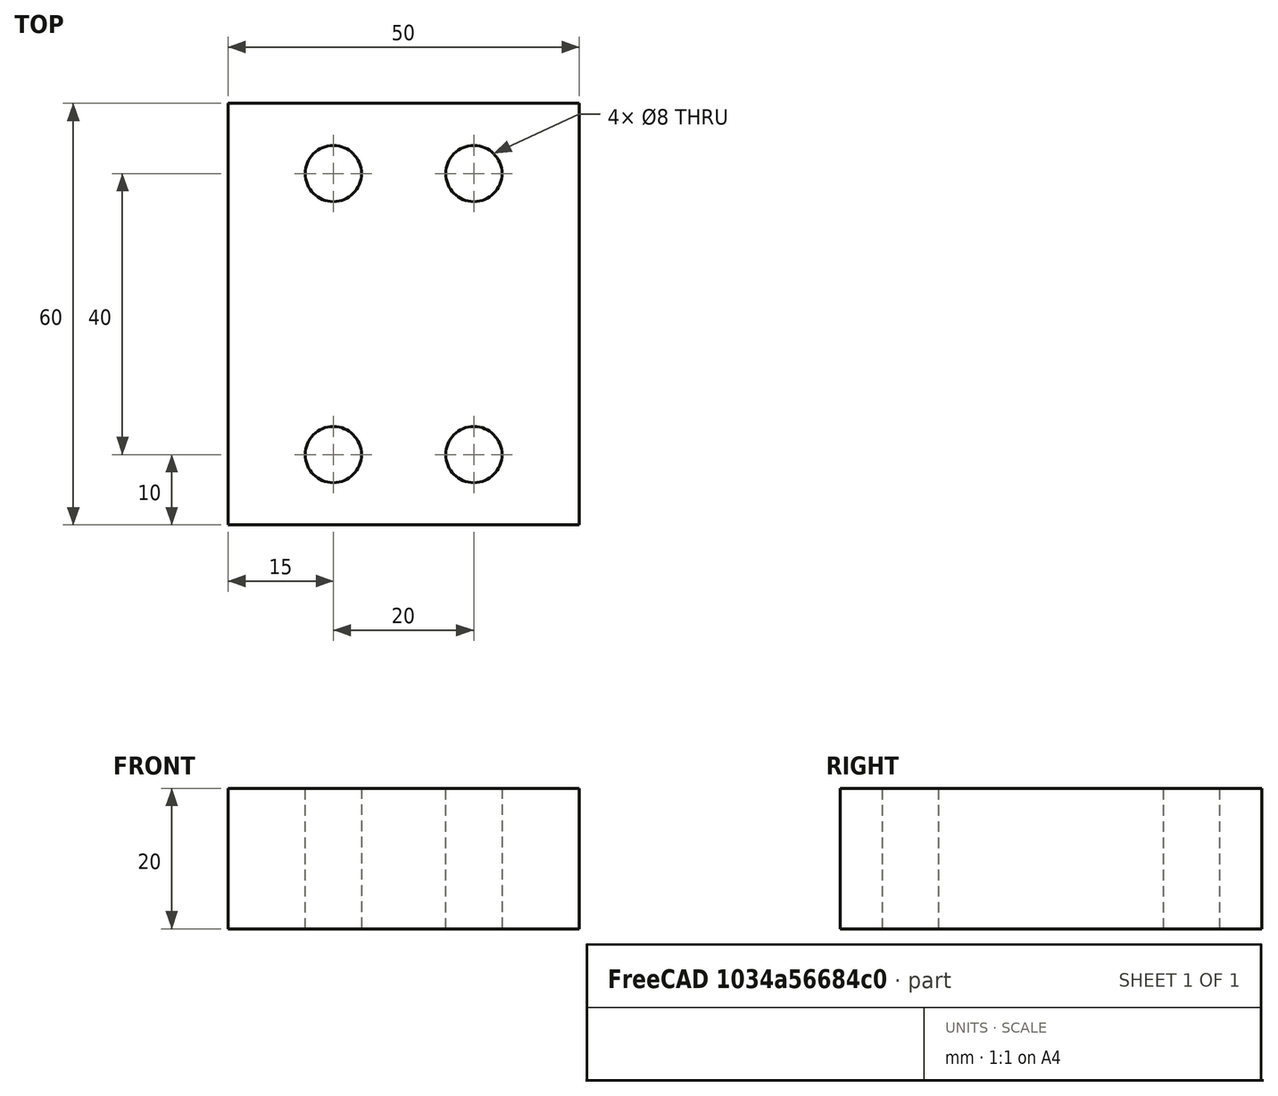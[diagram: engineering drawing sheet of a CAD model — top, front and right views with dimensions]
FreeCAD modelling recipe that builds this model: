
FCSTD DOCUMENT  (FreeCAD 0.19R17089 +1543 (Git))
Label: import-link
License: All rights reserved
LicenseURL: http://en.wikipedia.org/wiki/All_rights_reserved
objects: App::FeaturePython×40, Part::FeaturePython×40, App::Link×10, App::LinkElement×8, Sketcher::SketchObject×1, PartDesign::Pad×1, PartDesign::Body×1, App::DocumentObjectGroup×1
note: 40 computed .brp shape members not serialized (recipe doc carries the construction recipe); baked Part::Feature solids carry a one-line shape summary decoded from their .brp
EXTERNAL_REF file=xrepo-lib-003.FCStd obj=Assembly
EXTERNAL_REF file=xrepo-lib-003.FCStd obj=Assembly001
EXTERNAL_REF file=xrepo-lib-003.FCStd obj=Assembly002

FEATURE [Sketcher::SketchObject] Sketch006
  MapMode = 5
  Support = -> [XY_Plane003]
  sketch-geometry (8):
    g0: Circle CenterX=-10 CenterY=20 CenterZ=0 NormalX=0 NormalY=0 NormalZ=1 AngleXU=0 Radius=4
    g1: Circle CenterX=10 CenterY=20 CenterZ=0 NormalX=0 NormalY=0 NormalZ=1 AngleXU=0 Radius=4
    g2: Circle CenterX=10 CenterY=-20 CenterZ=0 NormalX=0 NormalY=0 NormalZ=1 AngleXU=0 Radius=4
    g3: Circle CenterX=-10 CenterY=-20 CenterZ=0 NormalX=0 NormalY=0 NormalZ=1 AngleXU=0 Radius=4
    g4: LineSegment StartX=-25 StartY=30 StartZ=0 EndX=25 EndY=30 EndZ=0
    g5: LineSegment StartX=25 StartY=30 StartZ=0 EndX=25 EndY=-30 EndZ=0
    g6: LineSegment StartX=25 StartY=-30 StartZ=0 EndX=-25 EndY=-30 EndZ=0
    g7: LineSegment StartX=-25 StartY=-30 StartZ=0 EndX=-25 EndY=30 EndZ=0
  constraints (19):
    c: Equal(g0,g1)
    c: Equal(g1,g2)
    c: Equal(g2,g3)
    c: Diameter(g0) = 8  'BHD'
    c: Symmetric(g0,g1,g-2)
    c: Symmetric(g1,g2,g-1)
    c: Symmetric(g0,g3,g-1)
    c: Coincident(g4,g5)
    c: Coincident(g5,g6)
    c: Coincident(g6,g7)
    c: Coincident(g7,g4)
    c: Horizontal(g6)
    c: Vertical(g7)
    c: Symmetric(g4,g4,g-2)
    c: Symmetric(g4,g5,g-1)
    c: Distance(g3,g2) = 20  'L1'
    c: Distance(g4) = 50  'L2'
    c: Distance(g1,g2) = 40  'W1'
    c: Distance(g7) = 60  'W2'
FEATURE [PartDesign::Pad] Pad005
  ClaimChildren = false
  Length = 20
  Length2 = 100
  Profile = -> Sketch006
  Reversed = true
  Type = 0
FEATURE [PartDesign::Body] Body003
  Group = -> [Sketch006,Pad005]
  Origin = -> Origin003
  Tip = -> Pad005
FEATURE [App::FeaturePython] Constraints003  # WARN: FeaturePython — macro-defined, semantics opaque (R4)
  GroupMode = 1
  _Version = 1
FEATURE [Part::FeaturePython] Parts003  # WARN: FeaturePython — macro-defined, semantics opaque (R4)
  Group = -> [Body003]
  GroupMode = 0
FEATURE [App::Link] Link  label="Assembly000 001"
  LinkPlacement = pos=(0,0,-2) rot=(0,0,1;0rad)
  LinkedObject = -> Link007
  Placement = pos=(0,0,-2) rot=(0,0,1;0rad)
FEATURE [App::Link] Link001  label="Assembly001 001"
  LinkedObject = -> Link008
FEATURE [Part::FeaturePython] Parts004  # WARN: FeaturePython — macro-defined, semantics opaque (R4)
  Group = -> [Link,Link001]
  GroupMode = 0
FEATURE [App::Link] Link002  label="Assembly000 002"
  LinkedObject = -> Link007
FEATURE [App::Link] Link003  label="Assembly002 001"
  LinkPlacement = pos=(0,0,2) rot=(0,0,1;0rad)
  LinkedObject = -> Link009
  Placement = pos=(0,0,2) rot=(0,0,1;0rad)
FEATURE [Part::FeaturePython] Parts005  # WARN: FeaturePython — macro-defined, semantics opaque (R4)
  Group = -> [Link002,Link003]
  GroupMode = 0
FEATURE [App::Link] Link004  label="Assembly003 001"
  LinkedObject = -> Assembly003
FEATURE [App::LinkElement] Link005_i0
  LinkPlacement = pos=(-10,20,0) rot=(0,0,1;0rad)
  LinkedObject = -> Assembly005
  Placement = pos=(-10,20,0) rot=(0,0,1;0rad)
FEATURE [App::LinkElement] Link005_i1
  LinkPlacement = pos=(10,20,0) rot=(0,0,1;0rad)
  LinkedObject = -> Assembly005
  Placement = pos=(10,20,0) rot=(0,0,1;0rad)
FEATURE [App::LinkElement] Link005_i2
  LinkPlacement = pos=(10,-20,0) rot=(0,0,1;0rad)
  LinkedObject = -> Assembly005
  Placement = pos=(10,-20,0) rot=(0,0,1;0rad)
FEATURE [App::LinkElement] Link005_i3
  LinkPlacement = pos=(-10,-20,0) rot=(0,0,1;0rad)
  LinkedObject = -> Assembly005
  Placement = pos=(-10,-20,0) rot=(0,0,1;0rad)
FEATURE [App::Link] Link005  label="Assembly005 001"
  ElementCount = 4
  ElementList = -> [Link005_i0,Link005_i1,Link005_i2,Link005_i3]
  LinkedObject = -> Assembly005
FEATURE [App::LinkElement] Link006_i0
  LinkPlacement = pos=(10,20,-33) rot=(0,-1,0;0rad)
  LinkedObject = -> Assembly004
  Placement = pos=(10,20,-33) rot=(0,-1,0;0rad)
FEATURE [App::LinkElement] Link006_i1
  LinkPlacement = pos=(-10,20,-33) rot=(0,-1,0;0rad)
  LinkedObject = -> Assembly004
  Placement = pos=(-10,20,-33) rot=(0,-1,0;0rad)
FEATURE [App::LinkElement] Link006_i2
  LinkPlacement = pos=(-10,-20,-33) rot=(0,-1,0;0rad)
  LinkedObject = -> Assembly004
  Placement = pos=(-10,-20,-33) rot=(0,-1,0;0rad)
FEATURE [App::LinkElement] Link006_i3
  LinkPlacement = pos=(10,-20,-33) rot=(0,-1,0;0rad)
  LinkedObject = -> Assembly004
  Placement = pos=(10,-20,-33) rot=(0,-1,0;0rad)
FEATURE [App::Link] Link006  label="Assembly004 001"
  ElementCount = 4
  ElementList = -> [Link006_i0,Link006_i1,Link006_i2,Link006_i3]
  LinkPlacement = pos=(8.1e-13,6.55651e-06,-55) rot=(0,1,0;3.14159rad)
  LinkedObject = -> Assembly004
  Placement = pos=(8.1e-13,6.55651e-06,-55) rot=(0,1,0;3.14159rad)
FEATURE [Part::FeaturePython] Parts006  # WARN: FeaturePython — macro-defined, semantics opaque (R4)
  Group = -> [Link004,Link005,Link006]
  GroupMode = 0
FEATURE [App::Link] Link007  label="Assembly000 003"
  LinkedObject = -> <external xrepo-lib-003.FCStd>#Assembly
FEATURE [App::Link] Link008  label="Assembly001 002"
  LinkedObject = -> <external xrepo-lib-003.FCStd>#Assembly001
FEATURE [App::Link] Link009  label="Assembly002 002"
  LinkedObject = -> <external xrepo-lib-003.FCStd>#Assembly002
FEATURE [App::DocumentObjectGroup] Group  label="Repository"
  Group = -> [Link007,Link008,Link009,Assembly003,Assembly004,Assembly005]
FEATURE [Part::FeaturePython] Assembly003  label="Assembly003 000"  # WARN: FeaturePython — macro-defined, semantics opaque (R4)
  AutoRelax = true
  BuildShape = 0
  Freeze = false
  Group = -> [Constraints003,Elements003,Parts003]
  GroupMode = 1
  SolverType = 1
  Verbose = false
  _SolverType = 1
  _Version = 1
FEATURE [App::FeaturePython] Elements003  # WARN: FeaturePython — macro-defined, semantics opaque (R4)
  Group = -> [Element005,Element006,Element007,Element008,Element009,Element010,Element011,Element012,Element015]
  GroupMode = 1
FEATURE [Part::FeaturePython] Element005  # link proxy (typed FeaturePython)
  Detach = false
  LinkTransform = true
  LinkedObject = -> Body003 [Pad005.Edge23]
  _Parent = -> Elements003
FEATURE [Part::FeaturePython] Element006  # link proxy (typed FeaturePython)
  Detach = false
  LinkTransform = true
  LinkedObject = -> Body003 [Pad005.Edge20]
  _Parent = -> Elements003
FEATURE [Part::FeaturePython] Element007  # link proxy (typed FeaturePython)
  Detach = false
  LinkTransform = true
  LinkedObject = -> Body003 [Pad005.Edge17]
  _Parent = -> Elements003
FEATURE [Part::FeaturePython] Element008  # link proxy (typed FeaturePython)
  Detach = false
  LinkTransform = true
  LinkedObject = -> Body003 [Pad005.Edge14]
  _Parent = -> Elements003
FEATURE [Part::FeaturePython] Element009  # link proxy (typed FeaturePython)
  Detach = false
  LinkTransform = true
  LinkedObject = -> Body003 [Pad005.Edge24]
  _Parent = -> Elements003
FEATURE [Part::FeaturePython] Element010  # link proxy (typed FeaturePython)
  Detach = false
  LinkTransform = true
  LinkedObject = -> Body003 [Pad005.Edge21]
  _Parent = -> Elements003
FEATURE [Part::FeaturePython] Element011  # link proxy (typed FeaturePython)
  Detach = false
  LinkTransform = true
  LinkedObject = -> Body003 [Pad005.Edge18]
  _Parent = -> Elements003
FEATURE [Part::FeaturePython] Element012  # link proxy (typed FeaturePython)
  Detach = false
  LinkTransform = true
  LinkedObject = -> Body003 [Pad005.Edge15]
  _Parent = -> Elements003
FEATURE [Part::FeaturePython] Assembly004  label="Assembly004 000"  # WARN: FeaturePython — macro-defined, semantics opaque (R4)
  AutoRelax = true
  BuildShape = 0
  Freeze = false
  Group = -> [Constraints004,Elements004,Parts004]
  GroupMode = 1
  SolverType = 1
  Verbose = false
  _SolverType = 1
  _Version = 1
FEATURE [App::FeaturePython] Constraints004  # WARN: FeaturePython — macro-defined, semantics opaque (R4)
  Group = -> [Constraint]
  GroupMode = 1
  _Version = 1
FEATURE [App::FeaturePython] Elements004  # WARN: FeaturePython — macro-defined, semantics opaque (R4)
  Group = -> [_Element,_Element001,Element013]
  GroupMode = 1
FEATURE [App::FeaturePython] Constraint  label="PlaneCoincident"  # WARN: FeaturePython — macro-defined, semantics opaque (R4)
  Angle = 0
  AnglePitch = 0
  AngleRoll = 0
  Cascade = false
  ConstraintType = 2
  Disabled = false
  Group = -> [ElementLink,ElementLink001]
  GroupMode = 1
  LockAngle = false
  Multiply = false
  OffsetX = 0
  OffsetY = 0
  _ConstraintType = 35
  _Parent = -> Constraints004
FEATURE [App::FeaturePython] ElementLink  label="_Element"  # link proxy (typed FeaturePython)
  LinkTransform = true
  LinkedObject = -> _Element
  _Parent = -> Constraint
FEATURE [Part::FeaturePython] _Element  # link proxy (typed FeaturePython)
  Detach = false
  LinkTransform = true
  LinkedObject = -> Link001 [1.$Element002.]
  _Parent = -> Elements004
FEATURE [App::FeaturePython] ElementLink001  label="_Element001"  # link proxy (typed FeaturePython)
  LinkTransform = true
  LinkedObject = -> _Element001
  _Parent = -> Constraint
FEATURE [Part::FeaturePython] _Element001  # link proxy (typed FeaturePython)
  Detach = false
  LinkTransform = true
  LinkedObject = -> Link [1.$Element001.]
  _Parent = -> Elements004
FEATURE [Part::FeaturePython] Element013  # link proxy (typed FeaturePython)
  Detach = false
  LinkTransform = true
  LinkedObject = -> Link [1.$Element.]
  _Parent = -> Elements004
FEATURE [Part::FeaturePython] Assembly005  label="Assembly005 000"  # WARN: FeaturePython — macro-defined, semantics opaque (R4)
  AutoRelax = true
  BuildShape = 0
  Freeze = false
  Group = -> [Constraints005,Elements005,Parts005]
  GroupMode = 1
  SolverType = 1
  Verbose = false
  _SolverType = 1
  _Version = 1
FEATURE [App::FeaturePython] Constraints005  # WARN: FeaturePython — macro-defined, semantics opaque (R4)
  Group = -> [Constraint001]
  GroupMode = 1
  _Version = 1
FEATURE [App::FeaturePython] Elements005  # WARN: FeaturePython — macro-defined, semantics opaque (R4)
  Group = -> [_Element002,_Element003,Element014]
  GroupMode = 1
FEATURE [App::FeaturePython] Constraint001  label="PlaneCoincident001"  # WARN: FeaturePython — macro-defined, semantics opaque (R4)
  Angle = 0
  AnglePitch = 0
  AngleRoll = 0
  Cascade = false
  ConstraintType = 2
  Disabled = false
  Group = -> [ElementLink002,ElementLink003]
  GroupMode = 1
  LockAngle = false
  Multiply = false
  OffsetX = 0
  OffsetY = 0
  _ConstraintType = 35
  _Parent = -> Constraints005
FEATURE [App::FeaturePython] ElementLink002  label="_Element002"  # link proxy (typed FeaturePython)
  LinkTransform = true
  LinkedObject = -> _Element002
  _Parent = -> Constraint001
FEATURE [Part::FeaturePython] _Element002  # link proxy (typed FeaturePython)
  Detach = false
  LinkTransform = true
  LinkedObject = -> Link002 [1.$Element001.]
  _Parent = -> Elements005
FEATURE [App::FeaturePython] ElementLink003  label="_Element003"  # link proxy (typed FeaturePython)
  LinkTransform = true
  LinkedObject = -> _Element003
  _Parent = -> Constraint001
FEATURE [Part::FeaturePython] _Element003  # link proxy (typed FeaturePython)
  Detach = false
  LinkTransform = true
  LinkedObject = -> Link003 [1.$Element004.]
  _Parent = -> Elements005
FEATURE [Part::FeaturePython] Element014  # link proxy (typed FeaturePython)
  Detach = false
  LinkTransform = true
  LinkedObject = -> Link002 [1.$Element.]
  _Parent = -> Elements005
FEATURE [Part::FeaturePython] Assembly006  label="Assembly006 000"  # WARN: FeaturePython — macro-defined, semantics opaque (R4)
  AutoRelax = true
  BuildShape = 0
  Freeze = false
  Group = -> [Constraints006,Elements006,Parts006]
  GroupMode = 1
  SolverType = 1
  Verbose = false
  _SolverType = 1
  _Version = 1
FEATURE [App::FeaturePython] Constraints006  # WARN: FeaturePython — macro-defined, semantics opaque (R4)
  Group = -> [Constraint002,Constraint003,Constraint004,Constraint005,Constraint006,Constraint007,Constraint008,Constraint009,Constraint010]
  GroupMode = 1
  _Version = 1
FEATURE [App::FeaturePython] Elements006  # WARN: FeaturePython — macro-defined, semantics opaque (R4)
  Group = -> [_Element004,_Element005,_Element006,_Element007,_Element008,_Element009,_Element010,_Element011,_Element012,_Element013,_Element014,_Element015,_Element016,_Element017,_Element018,_Element019,_Element020]
  GroupMode = 1
FEATURE [App::FeaturePython] Constraint002  label="Locked"  # WARN: FeaturePython — macro-defined, semantics opaque (R4)
  ConstraintType = 0
  Disabled = false
  Group = -> [ElementLink004]
  GroupMode = 1
  _ConstraintType = 0
  _Parent = -> Constraints006
FEATURE [App::FeaturePython] ElementLink004  label="_Element004"  # link proxy (typed FeaturePython)
  LinkTransform = true
  LinkedObject = -> _Element004
  _Parent = -> Constraint002
FEATURE [Part::FeaturePython] Element015  # link proxy (typed FeaturePython)
  Detach = false
  LinkTransform = true
  LinkedObject = -> Body003 [Pad005.Face9]
  _Parent = -> Elements003
FEATURE [Part::FeaturePython] _Element004  # link proxy (typed FeaturePython)
  Detach = false
  LinkTransform = true
  LinkedObject = -> Link004 [1.$Element015.]
  _Parent = -> Elements006
FEATURE [App::FeaturePython] Constraint003  label="PlaneCoincident002"  # WARN: FeaturePython — macro-defined, semantics opaque (R4)
  Angle = 0
  AnglePitch = 0
  AngleRoll = 0
  Cascade = false
  ConstraintType = 2
  Disabled = false
  Group = -> [ElementLink005,ElementLink006]
  GroupMode = 1
  LockAngle = false
  Multiply = false
  OffsetX = 0
  OffsetY = 0
  _ConstraintType = 35
  _Parent = -> Constraints006
FEATURE [App::FeaturePython] ElementLink005  label="_Element005"  # link proxy (typed FeaturePython)
  LinkTransform = true
  LinkedObject = -> _Element005
  _Parent = -> Constraint003
FEATURE [Part::FeaturePython] _Element005  # link proxy (typed FeaturePython)
  Detach = false
  LinkTransform = true
  LinkedObject = -> Link005 [Link005_i0.1.$Element014.]
  _Parent = -> Elements006
FEATURE [App::FeaturePython] ElementLink006  label="_Element006"  # link proxy (typed FeaturePython)
  LinkTransform = true
  LinkedObject = -> _Element006
  _Parent = -> Constraint003
FEATURE [Part::FeaturePython] _Element006  # link proxy (typed FeaturePython)
  Detach = false
  LinkTransform = true
  LinkedObject = -> Link004 [1.$Element005.]
  _Parent = -> Elements006
FEATURE [App::FeaturePython] Constraint004  label="PlaneCoincident003"  # WARN: FeaturePython — macro-defined, semantics opaque (R4)
  Angle = 0
  AnglePitch = 0
  AngleRoll = 0
  Cascade = false
  ConstraintType = 2
  Disabled = false
  Group = -> [ElementLink007,ElementLink008]
  GroupMode = 1
  LockAngle = false
  Multiply = false
  OffsetX = 0
  OffsetY = 0
  _ConstraintType = 35
  _Parent = -> Constraints006
FEATURE [App::FeaturePython] ElementLink007  label="_Element007"  # link proxy (typed FeaturePython)
  LinkTransform = true
  LinkedObject = -> _Element007
  _Parent = -> Constraint004
FEATURE [Part::FeaturePython] _Element007  # link proxy (typed FeaturePython)
  Detach = false
  LinkTransform = true
  LinkedObject = -> Link004 [1.$Element006.]
  _Parent = -> Elements006
FEATURE [App::FeaturePython] ElementLink008  label="_Element008"  # link proxy (typed FeaturePython)
  LinkTransform = true
  LinkedObject = -> _Element008
  _Parent = -> Constraint004
FEATURE [Part::FeaturePython] _Element008  # link proxy (typed FeaturePython)
  Detach = false
  LinkTransform = true
  LinkedObject = -> Link005 [Link005_i1.1.$Element014.]
  _Parent = -> Elements006
FEATURE [App::FeaturePython] Constraint005  label="PlaneCoincident004"  # WARN: FeaturePython — macro-defined, semantics opaque (R4)
  Angle = 0
  AnglePitch = 0
  AngleRoll = 0
  Cascade = false
  ConstraintType = 2
  Disabled = false
  Group = -> [ElementLink009,ElementLink010]
  GroupMode = 1
  LockAngle = false
  Multiply = false
  OffsetX = 0
  OffsetY = 0
  _ConstraintType = 35
  _Parent = -> Constraints006
FEATURE [App::FeaturePython] ElementLink009  label="_Element009"  # link proxy (typed FeaturePython)
  LinkTransform = true
  LinkedObject = -> _Element009
  _Parent = -> Constraint005
FEATURE [Part::FeaturePython] _Element009  # link proxy (typed FeaturePython)
  Detach = false
  LinkTransform = true
  LinkedObject = -> Link004 [1.$Element007.]
  _Parent = -> Elements006
FEATURE [App::FeaturePython] ElementLink010  label="_Element010"  # link proxy (typed FeaturePython)
  LinkTransform = true
  LinkedObject = -> _Element010
  _Parent = -> Constraint005
FEATURE [Part::FeaturePython] _Element010  # link proxy (typed FeaturePython)
  Detach = false
  LinkTransform = true
  LinkedObject = -> Link005 [Link005_i2.1.$Element014.]
  _Parent = -> Elements006
FEATURE [App::FeaturePython] Constraint006  label="PlaneCoincident005"  # WARN: FeaturePython — macro-defined, semantics opaque (R4)
  Angle = 0
  AnglePitch = 0
  AngleRoll = 0
  Cascade = false
  ConstraintType = 2
  Disabled = false
  Group = -> [ElementLink011,ElementLink012]
  GroupMode = 1
  LockAngle = false
  Multiply = false
  OffsetX = 0
  OffsetY = 0
  _ConstraintType = 35
  _Parent = -> Constraints006
FEATURE [App::FeaturePython] ElementLink011  label="_Element011"  # link proxy (typed FeaturePython)
  LinkTransform = true
  LinkedObject = -> _Element011
  _Parent = -> Constraint006
FEATURE [Part::FeaturePython] _Element011  # link proxy (typed FeaturePython)
  Detach = false
  LinkTransform = true
  LinkedObject = -> Link004 [1.$Element008.]
  _Parent = -> Elements006
FEATURE [App::FeaturePython] ElementLink012  label="_Element012"  # link proxy (typed FeaturePython)
  LinkTransform = true
  LinkedObject = -> _Element012
  _Parent = -> Constraint006
FEATURE [Part::FeaturePython] _Element012  # link proxy (typed FeaturePython)
  Detach = false
  LinkTransform = true
  LinkedObject = -> Link005 [Link005_i3.1.$Element014.]
  _Parent = -> Elements006
FEATURE [App::FeaturePython] Constraint007  label="PlaneCoincident006"  # WARN: FeaturePython — macro-defined, semantics opaque (R4)
  Angle = 0
  AnglePitch = 0
  AngleRoll = 0
  Cascade = false
  ConstraintType = 2
  Disabled = false
  Group = -> [ElementLink013,ElementLink014]
  GroupMode = 1
  LockAngle = false
  Multiply = false
  OffsetX = 0
  OffsetY = 0
  _ConstraintType = 35
  _Parent = -> Constraints006
FEATURE [App::FeaturePython] ElementLink013  label="_Element013"  # link proxy (typed FeaturePython)
  LinkTransform = true
  LinkedObject = -> _Element013
  _Parent = -> Constraint007
FEATURE [Part::FeaturePython] _Element013  # link proxy (typed FeaturePython)
  Detach = false
  LinkTransform = true
  LinkedObject = -> Link004 [1.$Element009.]
  _Parent = -> Elements006
FEATURE [App::FeaturePython] ElementLink014  label="_Element014"  # link proxy (typed FeaturePython)
  LinkTransform = true
  LinkedObject = -> _Element014
  _Parent = -> Constraint007
FEATURE [Part::FeaturePython] _Element014  # link proxy (typed FeaturePython)
  Detach = false
  LinkTransform = true
  LinkedObject = -> Link006 [Link006_i0.1.$Element013.]
  _Parent = -> Elements006
FEATURE [App::FeaturePython] Constraint008  label="PlaneCoincident007"  # WARN: FeaturePython — macro-defined, semantics opaque (R4)
  Angle = 0
  AnglePitch = 0
  AngleRoll = 0
  Cascade = false
  ConstraintType = 2
  Disabled = false
  Group = -> [ElementLink015,ElementLink016]
  GroupMode = 1
  LockAngle = false
  Multiply = false
  OffsetX = 0
  OffsetY = 0
  _ConstraintType = 35
  _Parent = -> Constraints006
FEATURE [App::FeaturePython] ElementLink015  label="_Element015"  # link proxy (typed FeaturePython)
  LinkTransform = true
  LinkedObject = -> _Element015
  _Parent = -> Constraint008
FEATURE [Part::FeaturePython] _Element015  # link proxy (typed FeaturePython)
  Detach = false
  LinkTransform = true
  LinkedObject = -> Link004 [1.$Element010.]
  _Parent = -> Elements006
FEATURE [App::FeaturePython] ElementLink016  label="_Element016"  # link proxy (typed FeaturePython)
  LinkTransform = true
  LinkedObject = -> _Element016
  _Parent = -> Constraint008
FEATURE [Part::FeaturePython] _Element016  # link proxy (typed FeaturePython)
  Detach = false
  LinkTransform = true
  LinkedObject = -> Link006 [Link006_i1.1.$Element013.]
  _Parent = -> Elements006
FEATURE [App::FeaturePython] Constraint009  label="PlaneCoincident008"  # WARN: FeaturePython — macro-defined, semantics opaque (R4)
  Angle = 0
  AnglePitch = 0
  AngleRoll = 0
  Cascade = false
  ConstraintType = 2
  Disabled = false
  Group = -> [ElementLink017,ElementLink018]
  GroupMode = 1
  LockAngle = false
  Multiply = false
  OffsetX = 0
  OffsetY = 0
  _ConstraintType = 35
  _Parent = -> Constraints006
FEATURE [App::FeaturePython] ElementLink017  label="_Element017"  # link proxy (typed FeaturePython)
  LinkTransform = true
  LinkedObject = -> _Element017
  _Parent = -> Constraint009
FEATURE [Part::FeaturePython] _Element017  # link proxy (typed FeaturePython)
  Detach = false
  LinkTransform = true
  LinkedObject = -> Link004 [1.$Element011.]
  _Parent = -> Elements006
FEATURE [App::FeaturePython] ElementLink018  label="_Element018"  # link proxy (typed FeaturePython)
  LinkTransform = true
  LinkedObject = -> _Element018
  _Parent = -> Constraint009
FEATURE [Part::FeaturePython] _Element018  # link proxy (typed FeaturePython)
  Detach = false
  LinkTransform = true
  LinkedObject = -> Link006 [Link006_i2.1.$Element013.]
  _Parent = -> Elements006
FEATURE [App::FeaturePython] Constraint010  label="PlaneCoincident009"  # WARN: FeaturePython — macro-defined, semantics opaque (R4)
  Angle = 0
  AnglePitch = 0
  AngleRoll = 0
  Cascade = false
  ConstraintType = 2
  Disabled = false
  Group = -> [ElementLink019,ElementLink020]
  GroupMode = 1
  LockAngle = false
  Multiply = false
  OffsetX = 0
  OffsetY = 0
  _ConstraintType = 35
  _Parent = -> Constraints006
FEATURE [App::FeaturePython] ElementLink019  label="_Element019"  # link proxy (typed FeaturePython)
  LinkTransform = true
  LinkedObject = -> _Element019
  _Parent = -> Constraint010
FEATURE [Part::FeaturePython] _Element019  # link proxy (typed FeaturePython)
  Detach = false
  LinkTransform = true
  LinkedObject = -> Link004 [1.$Element012.]
  _Parent = -> Elements006
FEATURE [App::FeaturePython] ElementLink020  label="_Element020"  # link proxy (typed FeaturePython)
  LinkTransform = true
  LinkedObject = -> _Element020
  _Parent = -> Constraint010
FEATURE [Part::FeaturePython] _Element020  # link proxy (typed FeaturePython)
  Detach = false
  LinkTransform = true
  LinkedObject = -> Link006 [Link006_i3.1.$Element013.]
  _Parent = -> Elements006

RESOLVED EXTERNAL PARTS (link-assembly join: the EXTERNAL_REF files above that resolve inside this repo's crawl, each included once):
---- part xrepo-lib-003.FCStd = doc fcstd_cd6cd5374638 ----
FCSTD DOCUMENT  (FreeCAD 0.19R17089 +1543 (Git))
Label: xrepo-lib-003
License: All rights reserved
LicenseURL: http://en.wikipedia.org/wiki/All_rights_reserved
objects: Part::FeaturePython×14, Sketcher::SketchObject×9, App::FeaturePython×8, PartDesign::Pad×8, PartDesign::Body×4, PartDesign::Chamfer×2, PartDesign::Pocket×1
note: 43 computed .brp shape members not serialized (recipe doc carries the construction recipe); baked Part::Feature solids carry a one-line shape summary decoded from their .brp

FEATURE [App::FeaturePython] Constraints  # WARN: FeaturePython — macro-defined, semantics opaque (R4)
  GroupMode = 1
  _Version = 1
FEATURE [Sketcher::SketchObject] Sketch
  MapMode = 5
  Support = -> [XY_Plane]
  sketch-geometry (2):
    g0: Circle CenterX=0 CenterY=0 CenterZ=0 NormalX=0 NormalY=0 NormalZ=1 AngleXU=0 Radius=4.15
    g1: Circle CenterX=0 CenterY=0 CenterZ=0 NormalX=0 NormalY=0 NormalZ=1 AngleXU=0 Radius=8
  constraints (4):
    c: Coincident(g0,g-1)
    c: Coincident(g1,g0)
    c: Diameter(g0) = 8.3  'D1'
    c: Diameter(g1) = 16  'D2'
FEATURE [PartDesign::Pad] Pad
  ClaimChildren = false
  Length = 2
  Length2 = 100
  Profile = -> Sketch
  Type = 0
FEATURE [PartDesign::Body] Body
  Group = -> [Sketch,Pad]
  Origin = -> Origin
  Tip = -> Pad
FEATURE [Part::FeaturePython] Parts  # WARN: FeaturePython — macro-defined, semantics opaque (R4)
  Group = -> [Body]
  GroupMode = 0
FEATURE [App::FeaturePython] Constraints001  # WARN: FeaturePython — macro-defined, semantics opaque (R4)
  GroupMode = 1
  _Version = 1
FEATURE [Sketcher::SketchObject] Sketch001
  MapMode = 5
  Support = -> [XY_Plane001]
  sketch-geometry (8):
    g0: Circle CenterX=0 CenterY=0 CenterZ=0 NormalX=0 NormalY=0 NormalZ=1 AngleXU=0 Radius=4
    g1: LineSegment StartX=7.50496 StartY=0.0945881 StartZ=0 EndX=3.67056 EndY=6.54678 EndZ=0
    g2: LineSegment StartX=3.67056 StartY=6.54678 StartZ=0 EndX=-3.83439 EndY=6.45219 EndZ=0
    g3: LineSegment StartX=-3.83439 StartY=6.45219 StartZ=0 EndX=-7.50496 EndY=-0.0945881 EndZ=0
    g4: LineSegment StartX=-7.50496 StartY=-0.0945881 StartZ=0 EndX=-3.67056 EndY=-6.54678 EndZ=0
    g5: LineSegment StartX=-3.67056 StartY=-6.54678 StartZ=0 EndX=3.83439 EndY=-6.45219 EndZ=0
    g6: LineSegment StartX=3.83439 StartY=-6.45219 StartZ=0 EndX=7.50496 EndY=0.0945881 EndZ=0
    g7: Circle [constr] CenterX=0 CenterY=0 CenterZ=0 NormalX=0 NormalY=0 NormalZ=1 AngleXU=0 Radius=7.50555
  constraints (17):
    c: Coincident(g0,g-1)
    c: Diameter(g0) = 8  'D1'
    c: Coincident(g1,g2)
    c: Coincident(g2,g3)
    c: Coincident(g3,g4)
    c: Coincident(g4,g5)
    c: Coincident(g5,g6)
    c: Coincident(g6,g1)
    c: Equal(g1, g2-g6) x5
    c: PointOnObject(g1,g7)
    c: PointOnObject(g2,g7)
    c: PointOnObject(g3,g7)
    c: PointOnObject(g4,g7)
    c: PointOnObject(g5,g7)
    c: PointOnObject(g6,g7)
    c: Coincident(g7,g0)
    c: Distance(g1,g5) = 13  'WS'
FEATURE [PartDesign::Pad] Pad001
  ClaimChildren = false
  Length = 6.4
  Length2 = 100
  Profile = -> Sketch001
  Type = 0
FEATURE [PartDesign::Body] Body001
  Group = -> [Sketch001,Pad001]
  Origin = -> Origin001
  Tip = -> Pad001
FEATURE [Part::FeaturePython] Parts001  # WARN: FeaturePython — macro-defined, semantics opaque (R4)
  Group = -> [Body001]
  GroupMode = 0
FEATURE [App::FeaturePython] Constraints002  # WARN: FeaturePython — macro-defined, semantics opaque (R4)
  GroupMode = 1
  _Version = 1
FEATURE [Sketcher::SketchObject] Sketch004
  MapMode = 5
  Support = -> [XY_Plane002]
  sketch-geometry (1):
    g0: Circle CenterX=0 CenterY=0 CenterZ=0 NormalX=0 NormalY=0 NormalZ=1 AngleXU=0 Radius=6.5
  constraints (2):
    c: Coincident(g0,g-1)
    c: Diameter(g0) = 13  'DH'
FEATURE [Sketcher::SketchObject] Sketch002
  MapMode = 5
  Support = -> [XY_Plane002]
  sketch-geometry (1):
    g0: Circle CenterX=0 CenterY=0 CenterZ=0 NormalX=0 NormalY=0 NormalZ=1 AngleXU=0 Radius=4
  constraints (2):
    c: Coincident(g0,g-1)
    c: Diameter(g0) = 8  'D1'
FEATURE [PartDesign::Pad] Pad002
  ClaimChildren = false
  Length = 5
  Length2 = 100
  Profile = -> Sketch002
  Reversed = true
  Type = 0
FEATURE [Sketcher::SketchObject] Sketch003
  ExternalGeometry = -> [Pad002]
  MapMode = 5
  Placement = pos=(0,0,-5) rot=(1,0,0;3.14159rad)
  Support = -> [Pad002]
FEATURE [PartDesign::Pad] Pad003
  BaseFeature = -> Pad002
  ClaimChildren = false
  Length = 30
  Length2 = 100
  Profile = -> Sketch003
  Type = 0
FEATURE [PartDesign::Pad] Pad004
  BaseFeature = -> Pad003
  ClaimChildren = false
  Length = 6
  Length2 = 100
  Profile = -> Sketch004
  Type = 0
FEATURE [Sketcher::SketchObject] Sketch005
  MapMode = 5
  Placement = pos=(0,0,6) rot=(0,0,1;0rad)
  Support = -> [Pad004]
  sketch-geometry (7):
    g0: LineSegment StartX=3.4641 StartY=0 StartZ=0 EndX=1.73205 EndY=3 EndZ=0
    g1: LineSegment StartX=1.73205 StartY=3 StartZ=0 EndX=-1.73205 EndY=3 EndZ=0
    g2: LineSegment StartX=-1.73205 StartY=3 StartZ=0 EndX=-3.4641 EndY=0 EndZ=0
    g3: LineSegment StartX=-3.4641 StartY=0 StartZ=0 EndX=-1.73205 EndY=-3 EndZ=0
    g4: LineSegment StartX=-1.73205 StartY=-3 StartZ=0 EndX=1.73205 EndY=-3 EndZ=0
    g5: LineSegment StartX=1.73205 StartY=-3 StartZ=0 EndX=3.4641 EndY=0 EndZ=0
    g6: Circle [constr] CenterX=0 CenterY=0 CenterZ=0 NormalX=0 NormalY=0 NormalZ=1 AngleXU=0 Radius=3.4641
  constraints (16):
    c: Coincident(g0,g1)
    c: Coincident(g1,g2)
    c: Coincident(g2,g3)
    c: Coincident(g3,g4)
    c: Coincident(g4,g5)
    c: Coincident(g5,g0)
    c: Equal(g0, g1-g5) x5
    c: PointOnObject(g0,g6)
    c: PointOnObject(g1,g6)
    c: PointOnObject(g2,g6)
    c: PointOnObject(g3,g6)
    c: PointOnObject(g4,g6)
    c: PointOnObject(g5,g6)
    c: Coincident(g6,g-1)
    c: PointOnObject(g5,g-1)
    c: Distance(g0,g4) = 6  'WS'
FEATURE [PartDesign::Pocket] Pocket
  BaseFeature = -> Pad004
  ClaimChildren = false
  Length = 5
  Length2 = 100
  Profile = -> Sketch005
  Type = 0
FEATURE [PartDesign::Chamfer] Chamfer
  Base = -> Pocket [Edge6]
  BaseFeature = -> Pocket
  Size = 1.2
FEATURE [PartDesign::Body] Body002
  Group = -> [Sketch002,Pad002,Sketch003,Pad003,Sketch004,Pad004,Sketch005,Pocket,Chamfer]
  Origin = -> Origin002
  Tip = -> Chamfer
FEATURE [Part::FeaturePython] Parts002  # WARN: FeaturePython — macro-defined, semantics opaque (R4)
  Group = -> [Body002]
  GroupMode = 0
FEATURE [App::FeaturePython] Constraints003  # WARN: FeaturePython — macro-defined, semantics opaque (R4)
  GroupMode = 1
  _Version = 1
FEATURE [Sketcher::SketchObject] Sketch006
  MapMode = 5
  Support = -> [XY_Plane003]
  sketch-geometry (1):
    g0: Circle CenterX=0 CenterY=0 CenterZ=0 NormalX=0 NormalY=0 NormalZ=1 AngleXU=0 Radius=4
  constraints (2):
    c: Coincident(g0,g-1)
    c: Diameter(g0) = 8  'D1'
FEATURE [PartDesign::Pad] Pad005
  ClaimChildren = false
  Length = 5
  Length2 = 100
  Profile = -> Sketch006
  Reversed = true
  Type = 0
FEATURE [Sketcher::SketchObject] Sketch007
  ExternalGeometry = -> [Pad005]
  MapMode = 5
  Placement = pos=(0,0,-5) rot=(1,0,0;3.14159rad)
  Support = -> [Pad005]
FEATURE [PartDesign::Pad] Pad006
  BaseFeature = -> Pad005
  ClaimChildren = false
  Length = 30
  Length2 = 100
  Profile = -> Sketch007
  Type = 0
FEATURE [PartDesign::Chamfer] Chamfer001
  Base = -> Pad006 [Edge5]
  BaseFeature = -> Pad006
  Size = 1.2
FEATURE [Sketcher::SketchObject] Sketch008
  MapMode = 5
  Support = -> [XY_Plane003]
  sketch-geometry (7):
    g0: LineSegment StartX=7.50555 StartY=0 StartZ=0 EndX=3.75278 EndY=6.5 EndZ=0
    g1: LineSegment StartX=3.75278 StartY=6.5 StartZ=0 EndX=-3.75278 EndY=6.5 EndZ=0
    g2: LineSegment StartX=-3.75278 StartY=6.5 StartZ=0 EndX=-7.50555 EndY=3.3924e-11 EndZ=0
    g3: LineSegment StartX=-7.50555 StartY=3.3924e-11 StartZ=0 EndX=-3.75278 EndY=-6.5 EndZ=0
    g4: LineSegment StartX=-3.75278 StartY=-6.5 StartZ=0 EndX=3.75278 EndY=-6.5 EndZ=0
    g5: LineSegment StartX=3.75278 StartY=-6.5 StartZ=0 EndX=7.50555 EndY=0 EndZ=0
    g6: Circle [constr] CenterX=0 CenterY=0 CenterZ=0 NormalX=0 NormalY=0 NormalZ=1 AngleXU=0 Radius=7.50555
  constraints (16):
    c: Coincident(g0,g1)
    c: Coincident(g1,g2)
    c: Coincident(g2,g3)
    c: Coincident(g3,g4)
    c: Coincident(g4,g5)
    c: Coincident(g5,g0)
    c: Equal(g0, g1-g5) x5
    c: PointOnObject(g0,g6)
    c: PointOnObject(g1,g6)
    c: PointOnObject(g2,g6)
    c: PointOnObject(g3,g6)
    c: PointOnObject(g4,g6)
    c: PointOnObject(g5,g6)
    c: Coincident(g6,g-1)
    c: PointOnObject(g5,g-1)
    c: Distance(g0,g4) = 13  'WS'
FEATURE [PartDesign::Pad] Pad007
  BaseFeature = -> Chamfer001
  ClaimChildren = false
  Length = 6.4
  Length2 = 100
  Profile = -> Sketch008
  Type = 0
FEATURE [PartDesign::Body] Body003
  Group = -> [Sketch006,Pad005,Sketch007,Pad006,Chamfer001,Sketch008,Pad007]
  Origin = -> Origin003
  Tip = -> Pad007
FEATURE [Part::FeaturePython] Parts003  # WARN: FeaturePython — macro-defined, semantics opaque (R4)
  Group = -> [Body003]
  GroupMode = 0
FEATURE [Part::FeaturePython] Element  # link proxy (typed FeaturePython)
  Detach = false
  LinkTransform = true
  LinkedObject = -> Body [Pad.Edge5]
  _Parent = -> Elements
FEATURE [Part::FeaturePython] Element001  # link proxy (typed FeaturePython)
  Detach = false
  LinkTransform = true
  LinkedObject = -> Body [Pad.Edge6]
  _Parent = -> Elements
FEATURE [App::FeaturePython] Elements  # WARN: FeaturePython — macro-defined, semantics opaque (R4)
  Group = -> [Element,Element001]
  GroupMode = 1
FEATURE [Part::FeaturePython] Assembly  label="Assembly000 000"  # WARN: FeaturePython — macro-defined, semantics opaque (R4)
  AutoRelax = true
  BuildShape = 0
  Freeze = false
  Group = -> [Constraints,Elements,Parts]
  GroupMode = 1
  SolverType = 1
  Verbose = false
  _SolverType = 1
  _Version = 1
FEATURE [Part::FeaturePython] Element002  # link proxy (typed FeaturePython)
  Detach = false
  LinkTransform = true
  LinkedObject = -> Body001 [Pad001.Edge20]
  _Parent = -> Elements001
FEATURE [Part::FeaturePython] Element003  # link proxy (typed FeaturePython)
  Detach = false
  LinkTransform = true
  LinkedObject = -> Body001 [Pad001.Edge21]
  _Parent = -> Elements001
FEATURE [App::FeaturePython] Elements001  # WARN: FeaturePython — macro-defined, semantics opaque (R4)
  Group = -> [Element002,Element003]
  GroupMode = 1
FEATURE [Part::FeaturePython] Assembly001  label="Assembly001 000"  # WARN: FeaturePython — macro-defined, semantics opaque (R4)
  AutoRelax = true
  BuildShape = 0
  Freeze = false
  Group = -> [Constraints001,Elements001,Parts001]
  GroupMode = 1
  SolverType = 1
  Verbose = false
  _SolverType = 1
  _Version = 1
FEATURE [Part::FeaturePython] Element004  # link proxy (typed FeaturePython)
  Detach = false
  LinkTransform = true
  LinkedObject = -> Body002 [Pad002.Edge2]
  _Parent = -> Elements002
FEATURE [App::FeaturePython] Elements002  # WARN: FeaturePython — macro-defined, semantics opaque (R4)
  Group = -> [Element004]
  GroupMode = 1
FEATURE [Part::FeaturePython] Assembly002  label="Assembly002 000"  # WARN: FeaturePython — macro-defined, semantics opaque (R4)
  AutoRelax = true
  BuildShape = 0
  Freeze = false
  Group = -> [Constraints002,Elements002,Parts002]
  GroupMode = 1
  SolverType = 1
  Verbose = false
  _SolverType = 1
  _Version = 1
FEATURE [Part::FeaturePython] Assembly003  label="Assembly003 000"  # WARN: FeaturePython — macro-defined, semantics opaque (R4)
  AutoRelax = true
  BuildShape = 0
  Freeze = false
  Group = -> [Constraints003,Elements003,Parts003]
  GroupMode = 1
  SolverType = 1
  Verbose = false
  _SolverType = 1
  _Version = 1
FEATURE [App::FeaturePython] Elements003  # WARN: FeaturePython — macro-defined, semantics opaque (R4)
  Group = -> [Element005]
  GroupMode = 1
FEATURE [Part::FeaturePython] Element005  label="Element004"  # link proxy (typed FeaturePython)
  Detach = false
  LinkTransform = true
  LinkedObject = -> Body003 [Pad007.Edge7]
  _Parent = -> Elements003
